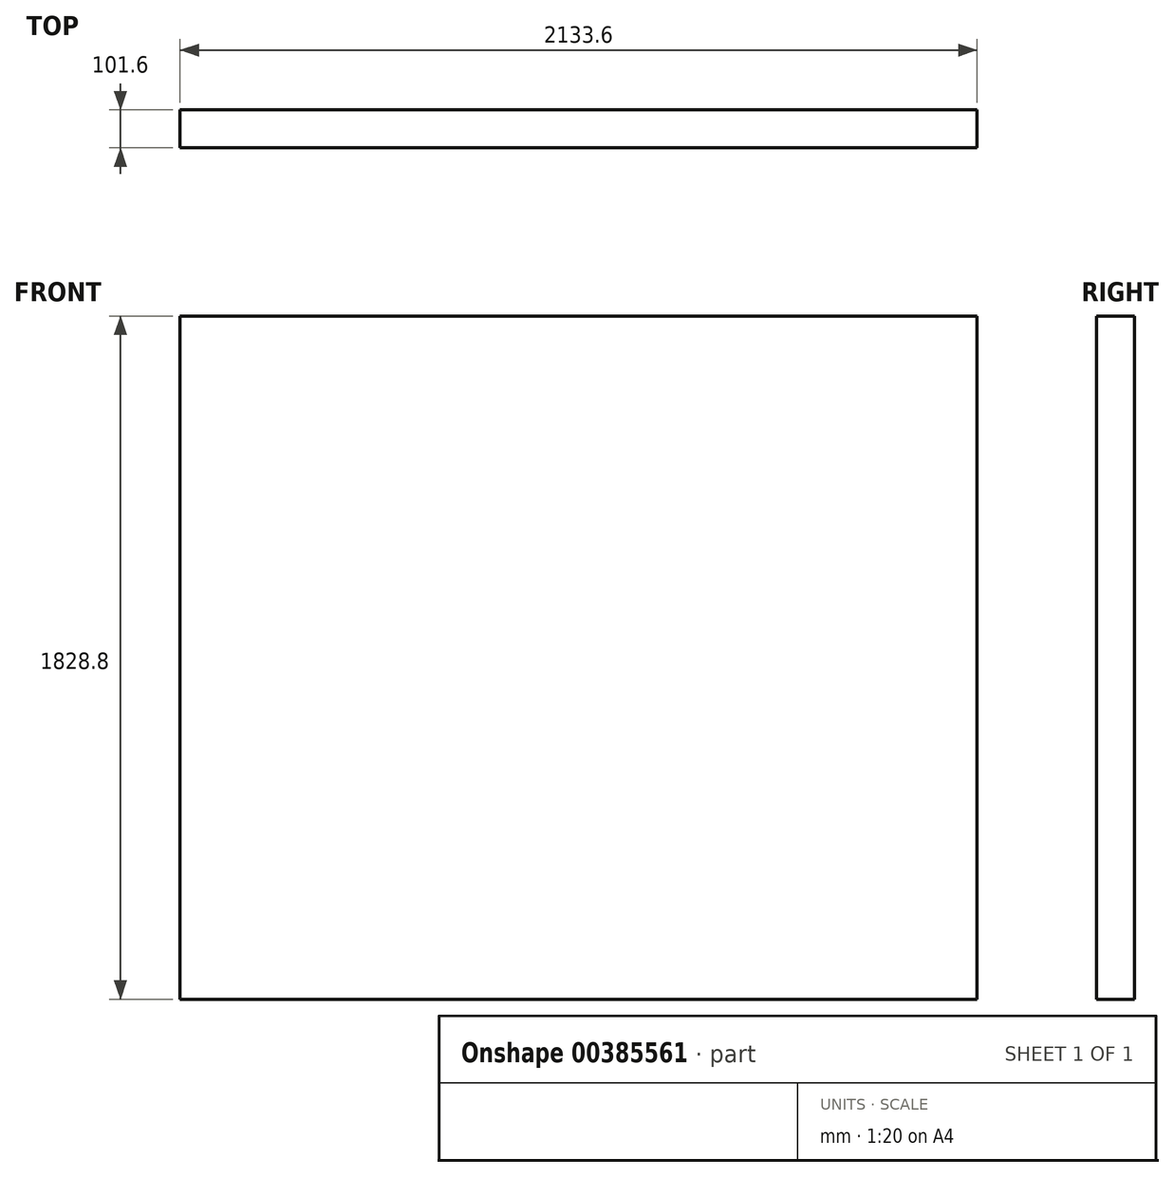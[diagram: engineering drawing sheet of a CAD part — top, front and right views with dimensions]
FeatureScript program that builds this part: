
annotation { "Feature Type Name" : "Feature", "Feature Type Description" : "" }
export const myFeature = defineFeature(function(context is Context, id is Id, definition is map)
    precondition{}
    {
        {
            var Q0;
            Q0=qCreatedBy(makeId("Front.planeOp"),FACE);
            var sketch = newSketch(context, id + "F0", { "sketchPlane" : qUnion([Q0])});
            skLineSegment(sketch, "E0.bottom", {"start": v(1066.8, -914.4) * mm, "end": v(-1066.8, -914.4) * mm});
            skLineSegment(sketch, "E0.top", {"start": v(1066.8, 914.4) * mm, "end": v(-1066.8, 914.4) * mm});
            skLineSegment(sketch, "E0.left", {"start": v(1066.8, -914.4) * mm, "end": v(1066.8, 914.4) * mm});
            skLineSegment(sketch, "E0.right", {"start": v(-1066.8, -914.4) * mm, "end": v(-1066.8, 914.4) * mm});
            skPoint(sketch, "E0.middle", {"position": v(0, 0) * mm});
            skSolve(sketch);
        }
        {
            var Q0;
            Q0=makeQuery(id+"F0.imprint","IMPRINT",FACE,{"disambiguationData":[TD([[makeQuery(id+"F0.imprint","IMPRINT",EDGE,{"derivedFrom":sQuery(id+"F0.wireOp",EDGE,"E0.bottom")}),-1.0]])]});
            extrude(context, id + "F1", {"entities" : qUnion([Q0]), "depth" : 101.6 * mm});
        }
    });
